# Revit family: Plymold-Essentials-Mesa_Booth_Double-
name_source: partatom
category: Furniture
units: mm (PartAtom-declared; Revit-internal decimal feet)

## family parameters
Always vertical = Yes
Cut with Voids When Loaded = No
OmniClass Number = 23.40.20.00
OmniClass Title = General Furniture and Specialties
Render Appearance Source = Family Geometry
Room Calculation Point = No
Shared = No
Work Plane-Based = No

## types (2) — shared parameters
Assembly Code = E2020200
BACK MATERIAL = PLY - Vinyl - Bluejay
BASE MATERIAL = PLY - Stainless Steel
Brand = Mesa & Vista Booths
CAP MATERIAL = PLY - UHMW, Black
CASTER MATERIAL = PLY - UHMW, Black
Default Elevation = 0"
Depth = 45"
FRAME MATERIAL = PLY - Stainless Steel
GLIDES MATERIAL = PLY - UHMW, Black
Height = 36"
Keynote = 12500
LEG MATERIAL = PLY - Stainless Steel
MECHANISM MATERIAL = PLY - Stainless Steel
Manufacturer = Plymold
POWER MATERIAL = PLY - UHMW, Black
Product Documentation Link = https://plymold.com
Revit Model Built By = https://www.servex-us.com
SEAT MATERIAL = PLY - Vinyl - Bluejay
SUPPORT MATERIAL = PLY - Stainless Steel
Sustainability = https://plymold.com
Type Comments = Booth Seating
URL = https://plymold.com
zero-valued in all types: Cost

## per-type parameters (varying)
| type | Description | Width |
| ME3648D | Mesa Booth Double - 48”W x 45”D x 36”H | 48" |
| ME3660D | Mesa Booth Double - 60”W x 45”D x 36”H | 60" |

note: column(s) folded — value = type name in every type: Model

## geometry (parser evidence)
native form markers: Sweep x20
no freeform markers — native parametric forms only
